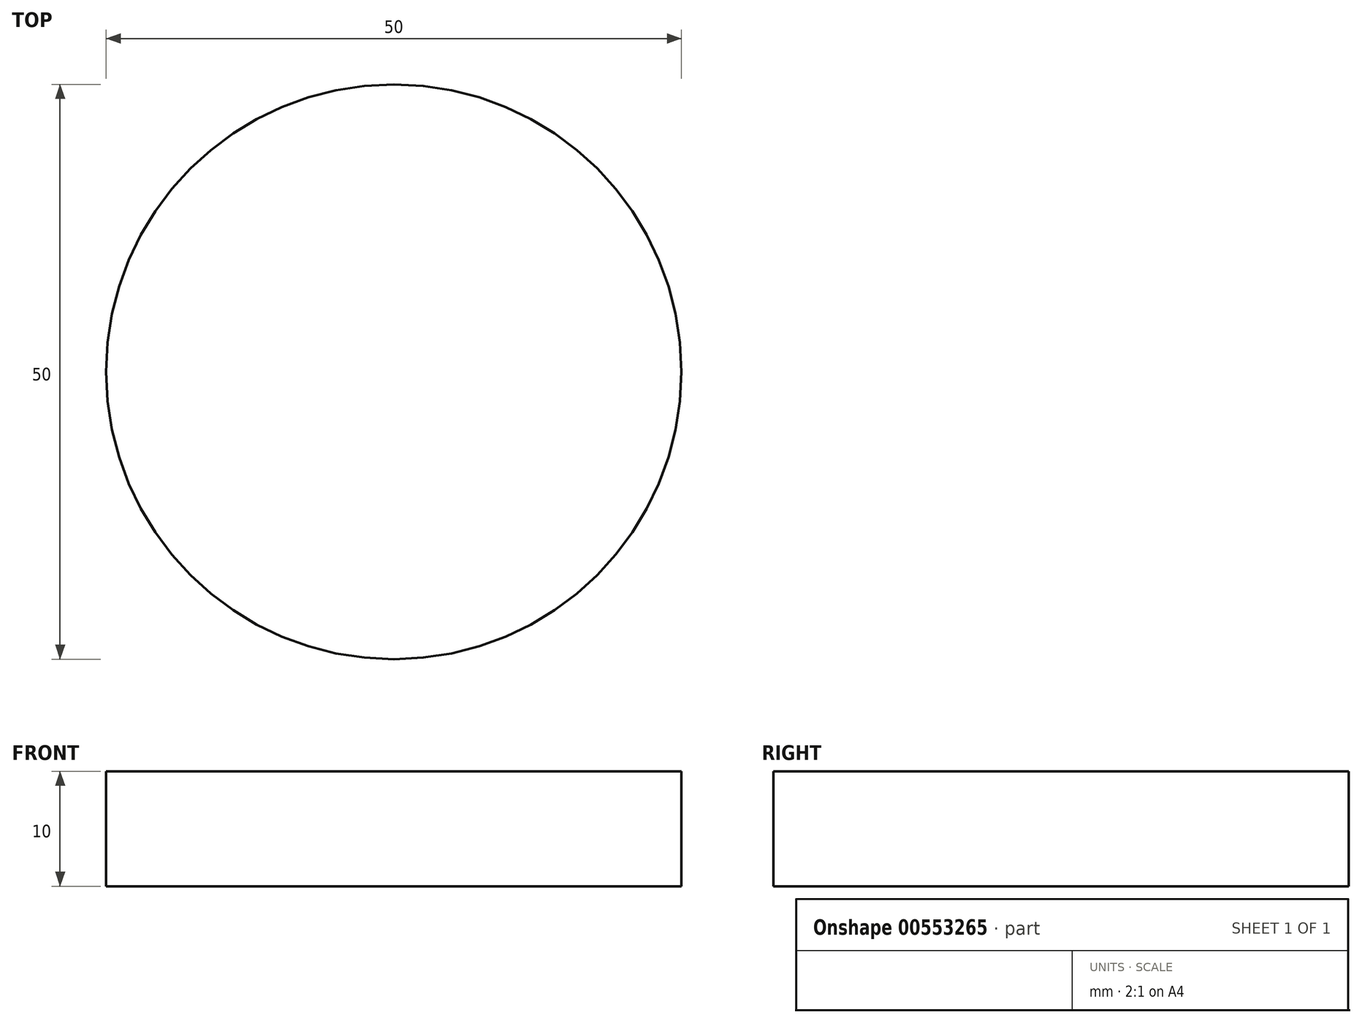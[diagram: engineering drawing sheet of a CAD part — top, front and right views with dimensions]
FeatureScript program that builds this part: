
annotation { "Feature Type Name" : "Feature", "Feature Type Description" : "" }
export const myFeature = defineFeature(function(context is Context, id is Id, definition is map)
    precondition{}
    {
        {
            var Q0;
            Q0=qCreatedBy(makeId("Top.planeOp"),FACE);
            var sketch = newSketch(context, id + "F0", { "sketchPlane" : qUnion([Q0])});
            skCircle(sketch, "E0", {"center": v(0, 0) * mm, "radius": 25 * mm});
            skSolve(sketch);
        }
        {
            var Q0;
            Q0 = qSketchRegion(id + "F0", true);
            extrude(context, id + "F1", {"entities" : qUnion([Q0]), "depth" : 10 * mm, "offsetDistance" : 25 * mm});
        }
    });
